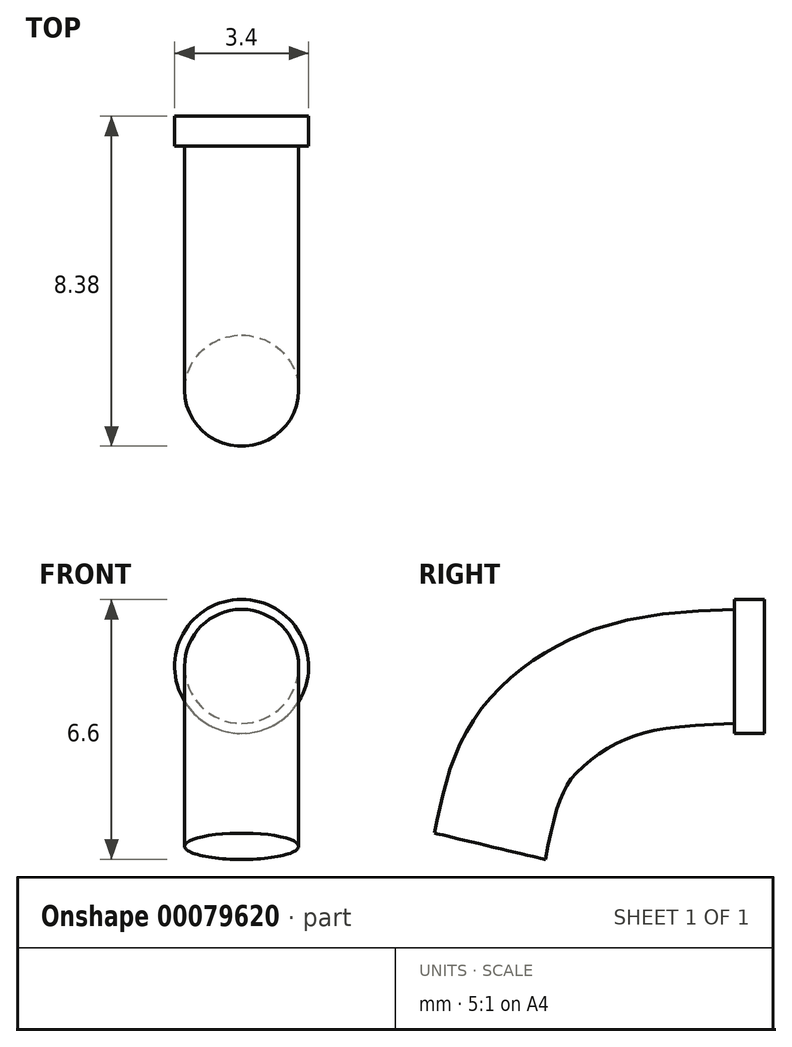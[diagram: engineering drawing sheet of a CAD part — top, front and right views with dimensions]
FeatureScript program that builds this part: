
annotation { "Feature Type Name" : "Feature", "Feature Type Description" : "" }
export const myFeature = defineFeature(function(context is Context, id is Id, definition is map)
    precondition{}
    {
        {
            var Q0;
            Q0=qCreatedBy(makeId("Front.planeOp"),FACE);
            var sketch = newSketch(context, id + "F0", { "sketchPlane" : qUnion([Q0])});
            skCircle(sketch, "E0", {"center": v(0, 4.57) * mm, "radius": 1.45 * mm});
            skSolve(sketch);
        }
        {
            var Q0;
            Q0=qCreatedBy(makeId("Right.planeOp"),FACE);
            var sketch = newSketch(context, id + "F1", { "sketchPlane" : qUnion([Q0])});
            skFitSpline(sketch, "E1", {"points": [v(0, 4.57) * mm, v(-3.41, 4.01) * mm, v(-5.4, 2.43) * mm, v(-6.2, 0) * mm], "startDerivative": vector(-13.38, -0.44) * mm, "endDerivative": vector(-1.7, -8.35) * mm});
            skSolve(sketch);
        }
        {
            var Q0;
            Q0 = qSketchRegion(id + "F0", true);
            var Q1;
            Q1=sQuery(id+"F1.wireOp",EDGE,"E1");
            sweep(context, id + "F2", {"profiles" : qUnion([Q0]), "path" : qUnion([Q1])});
        }
        {
            var Q0;
            Q0=makeQuery(id+"F2.opSweep","CAP_FACE",FACE,{"disambiguationData":[OSD([sQuery(id+"F0.wireOp",EDGE,"E0"),sQuery(id+"F1.wireOp",VERTEX,"E1.start")])],"isStart":true});
            var sketch = newSketch(context, id + "F3", { "sketchPlane" : qUnion([Q0])});
            skCircle(sketch, "E2", {"center": v(0, 4.57) * mm, "radius": 1.7 * mm});
            skSolve(sketch);
        }
        {
            var Q0;
            Q0 = qSketchRegion(id + "F3", true);
            extrude(context, id + "F4", {"entities" : qUnion([Q0]), "operationType" : NewBodyOperationType.ADD, "depth" : 0.76 * mm});
        }
    });
